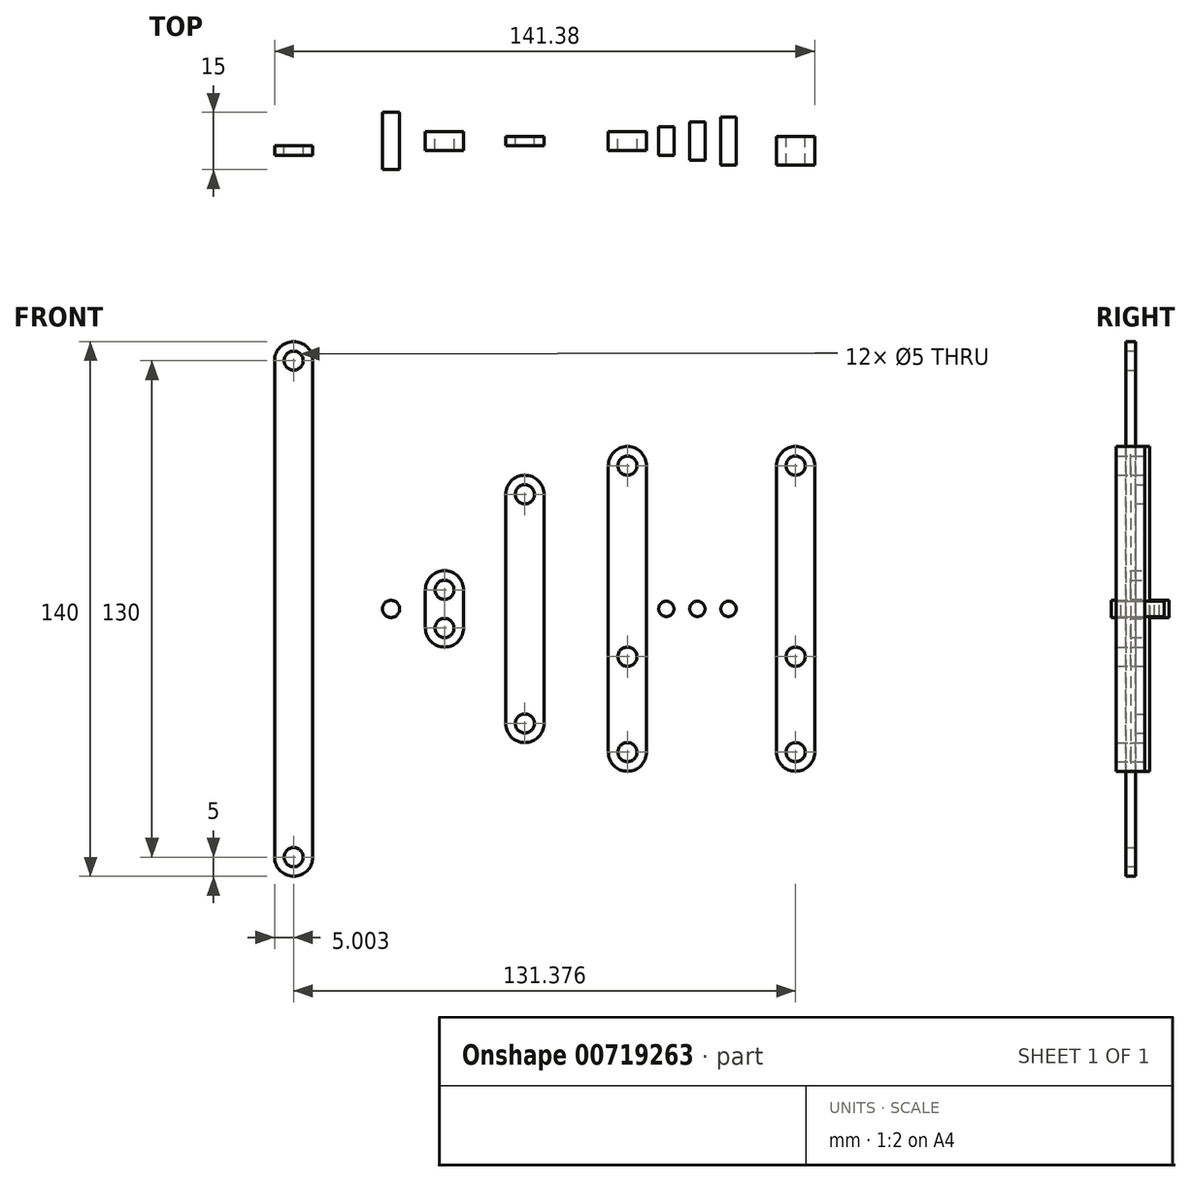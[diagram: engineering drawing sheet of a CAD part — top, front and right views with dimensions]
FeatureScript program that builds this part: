
annotation { "Feature Type Name" : "Feature", "Feature Type Description" : "" }
export const myFeature = defineFeature(function(context is Context, id is Id, definition is map)
    precondition{}
    {
        {
            assignVariable(context, id + "F0", {"name" : "pin1_len", "anyValue" : 7.5});
        }
        {
            assignVariable(context, id + "F1", {"name" : "pin2_len", "anyValue" : 10});
        }
        {
            var Q0;
            Q0=qCreatedBy(makeId("Front.planeOp"),FACE);
            var sketch = newSketch(context, id + "F2", { "sketchPlane" : qUnion([Q0])});
            skLineSegment(sketch, "E0", {"start": v(-5, 0) * mm, "end": v(5, 0) * mm, "construction": true});
            skArc(sketch, "E1", {"start": v(5, 37.5) * mm, "mid": v(0, 42.5) * mm, "end": v(-5, 37.5) * mm});
            skLineSegment(sketch, "E2", {"start": v(5, 37.5) * mm, "end": v(-5, 37.5) * mm, "construction": true});
            skLineSegment(sketch, "E3", {"start": v(-5, 37.5) * mm, "end": v(-5, 0) * mm});
            skLineSegment(sketch, "E4", {"start": v(5, 37.5) * mm, "end": v(5, 0) * mm});
            skCircle(sketch, "E5", {"center": v(0, 37.5) * mm, "radius": 2.5 * mm});
            skArc(sketch, "E6.MirrorCS", {"start": v(5, -37.5) * mm, "mid": v(0, -42.5) * mm, "end": v(-5, -37.5) * mm});
            skCircle(sketch, "E7.MirrorC", {"center": v(0, -37.5) * mm, "radius": 2.5 * mm});
            skLineSegment(sketch, "E8.MirrorCS", {"start": v(-5, -37.5) * mm, "end": v(-5, 0) * mm});
            skLineSegment(sketch, "E9.MirrorCS", {"start": v(5, -37.5) * mm, "end": v(5, 0) * mm});
            skCircle(sketch, "E10", {"center": v(0, -12.5) * mm, "radius": 2.5 * mm});
            skSolve(sketch);
        }
        {
            var Q0;
            Q0 = qSketchRegion(id + "F2", true);
            extrude(context, id + "F3", {"entities" : qUnion([Q0]), "depth" : 5 * mm, "offsetDistance" : 25 * mm, "symmetric" : true});
        }
        {
            var Q0;
            Q0=qCreatedBy(makeId("Front.planeOp"),FACE);
            var sketch = newSketch(context, id + "F4", { "sketchPlane" : qUnion([Q0])});
            skLineSegment(sketch, "E11", {"start": v(-31.86, 0) * mm, "end": v(-21.86, 0) * mm, "construction": true});
            skArc(sketch, "E12", {"start": v(-21.86, 30) * mm, "mid": v(-26.86, 35) * mm, "end": v(-31.86, 30) * mm});
            skLineSegment(sketch, "E13", {"start": v(-21.86, 30) * mm, "end": v(-31.86, 30) * mm, "construction": true});
            skLineSegment(sketch, "E14", {"start": v(-31.86, 30) * mm, "end": v(-31.86, 0) * mm});
            skLineSegment(sketch, "E15", {"start": v(-21.86, 30) * mm, "end": v(-21.86, 0) * mm});
            skCircle(sketch, "E16", {"center": v(-26.86, 30) * mm, "radius": 2.5 * mm});
            skArc(sketch, "E17.MirrorCS", {"start": v(-21.86, -30) * mm, "mid": v(-26.86, -35) * mm, "end": v(-31.86, -30) * mm});
            skCircle(sketch, "E18.MirrorC", {"center": v(-26.86, -30) * mm, "radius": 2.5 * mm});
            skLineSegment(sketch, "E19.MirrorCS", {"start": v(-31.86, -30) * mm, "end": v(-31.86, 0) * mm});
            skLineSegment(sketch, "E20.MirrorCS", {"start": v(-21.86, -30) * mm, "end": v(-21.86, 0) * mm});
            skSolve(sketch);
        }
        {
            var Q0;
            Q0 = qSketchRegion(id + "F4", true);
            extrude(context, id + "F5", {"entities" : qUnion([Q0]), "depth" : 2.5 * mm, "offsetDistance" : 25 * mm, "symmetric" : true});
        }
        {
            var Q0;
            Q0=qCreatedBy(makeId("Front.planeOp"),FACE);
            var sketch = newSketch(context, id + "F6", { "sketchPlane" : qUnion([Q0])});
            skLineSegment(sketch, "E21", {"start": v(-52.87, 0) * mm, "end": v(-42.87, 0) * mm, "construction": true});
            skArc(sketch, "E22", {"start": v(-42.87, 5) * mm, "mid": v(-47.87, 10) * mm, "end": v(-52.87, 5) * mm});
            skLineSegment(sketch, "E23", {"start": v(-42.87, 5) * mm, "end": v(-52.87, 5) * mm, "construction": true});
            skLineSegment(sketch, "E24", {"start": v(-52.87, 5) * mm, "end": v(-52.87, 0) * mm});
            skLineSegment(sketch, "E25", {"start": v(-42.87, 5) * mm, "end": v(-42.87, 0) * mm});
            skCircle(sketch, "E26", {"center": v(-47.87, 5) * mm, "radius": 2.5 * mm});
            skArc(sketch, "E27.MirrorCS", {"start": v(-42.87, -5) * mm, "mid": v(-47.87, -10) * mm, "end": v(-52.87, -5) * mm});
            skCircle(sketch, "E28.MirrorC", {"center": v(-47.87, -5) * mm, "radius": 2.5 * mm});
            skLineSegment(sketch, "E29.MirrorCS", {"start": v(-52.87, -5) * mm, "end": v(-52.87, 0) * mm});
            skLineSegment(sketch, "E30.MirrorCS", {"start": v(-42.87, -5) * mm, "end": v(-42.87, 0) * mm});
            skSolve(sketch);
        }
        {
            var Q0;
            Q0 = qSketchRegion(id + "F6", true);
            extrude(context, id + "F7", {"entities" : qUnion([Q0]), "depth" : 5 * mm, "offsetDistance" : 25 * mm, "symmetric" : true});
        }
        {
            var Q0;
            Q0=qCreatedBy(makeId("Front.planeOp"),FACE);
            var sketch = newSketch(context, id + "F8", { "sketchPlane" : qUnion([Q0])});
            skCircle(sketch, "E31", {"center": v(10.18, 0) * mm, "radius": 2 * mm});
            skSolve(sketch);
        }
        {
            var Q0;
            Q0 = qSketchRegion(id + "F8", true);
            extrude(context, id + "F9", {"entities" : qUnion([Q0]), "depth" : (getVariable(context, 'pin1_len')) * mm, "offsetDistance" : 25 * mm, "symmetric" : true});
        }
        {
            var Q0;
            Q0=qCreatedBy(makeId("Front.planeOp"),FACE);
            var sketch = newSketch(context, id + "F10", { "sketchPlane" : qUnion([Q0])});
            skCircle(sketch, "E32", {"center": v(18.3, 0) * mm, "radius": 2 * mm});
            skSolve(sketch);
        }
        {
            var Q0;
            Q0 = qSketchRegion(id + "F10", true);
            extrude(context, id + "F11", {"entities" : qUnion([Q0]), "depth" : (getVariable(context, 'pin2_len')) * mm, "offsetDistance" : 25 * mm, "symmetric" : true});
        }
        {
            var Q0;
            Q0=makeQuery(id+"F3.opExtrude","CAP_FACE",FACE,{"disambiguationData":[OSD([sQuery(id+"F2.wireOp",EDGE,"E1"),sQuery(id+"F2.wireOp",EDGE,"E3"),sQuery(id+"F2.wireOp",EDGE,"E4"),sQuery(id+"F2.wireOp",EDGE,"E5"),sQuery(id+"F2.wireOp",EDGE,"E6.MirrorCS"),sQuery(id+"F2.wireOp",EDGE,"E7.MirrorC"),sQuery(id+"F2.wireOp",EDGE,"E8.MirrorCS"),sQuery(id+"F2.wireOp",EDGE,"E9.MirrorCS"),sQuery(id+"F2.wireOp",EDGE,"E10")])],"isStart":false});
            var sketch = newSketch(context, id + "F12", { "sketchPlane" : qUnion([Q0])});
            skLineSegment(sketch, "E33", {"start": v(39, 0) * mm, "end": v(49, 0) * mm, "construction": true});
            skArc(sketch, "E34", {"start": v(49, 37.5) * mm, "mid": v(44, 42.5) * mm, "end": v(39, 37.5) * mm});
            skLineSegment(sketch, "E35", {"start": v(49, 37.5) * mm, "end": v(39, 37.5) * mm, "construction": true});
            skLineSegment(sketch, "E36", {"start": v(39, 37.5) * mm, "end": v(39, 0) * mm});
            skLineSegment(sketch, "E37", {"start": v(49, 37.5) * mm, "end": v(49, 0) * mm});
            skCircle(sketch, "E38", {"center": v(44, 37.5) * mm, "radius": 2.5 * mm});
            skArc(sketch, "E39.MirrorCS", {"start": v(49, -37.5) * mm, "mid": v(44, -42.5) * mm, "end": v(39, -37.5) * mm});
            skCircle(sketch, "E40.MirrorC", {"center": v(44, -37.5) * mm, "radius": 2.5 * mm});
            skLineSegment(sketch, "E41.MirrorCS", {"start": v(39, -37.5) * mm, "end": v(39, 0) * mm});
            skLineSegment(sketch, "E42.MirrorCS", {"start": v(49, -37.5) * mm, "end": v(49, 0) * mm});
            skCircle(sketch, "E43", {"center": v(44, -12.5) * mm, "radius": 2.5 * mm});
            skSolve(sketch);
        }
        {
            var Q0;
            Q0 = qSketchRegion(id + "F12", true);
            extrude(context, id + "F13", {"entities" : qUnion([Q0]), "depth" : 7.5 * mm, "offsetDistance" : 25 * mm, "symmetric" : true});
        }
        {
            var Q0;
            Q0=qCreatedBy(makeId("Front.planeOp"),FACE);
            var sketch = newSketch(context, id + "F14", { "sketchPlane" : qUnion([Q0])});
            skCircle(sketch, "E44", {"center": v(26.45, 0) * mm, "radius": 2 * mm});
            skSolve(sketch);
        }
        {
            var Q0;
            Q0=makeQuery(id+"F14.imprint","IMPRINT",FACE,{"disambiguationData":[TD([[makeQuery(id+"F14.imprint","IMPRINT",EDGE,{"derivedFrom":sQuery(id+"F14.wireOp",EDGE,"E44")}),1.0]])]});
            extrude(context, id + "F15", {"entities" : qUnion([Q0]), "depth" : 12.5 * mm, "offsetDistance" : 25 * mm, "symmetric" : true});
        }
        {
            var Q0;
            Q0=qCreatedBy(makeId("Front.planeOp"),FACE);
            var sketch = newSketch(context, id + "F16", { "sketchPlane" : qUnion([Q0])});
            skCircle(sketch, "E45", {"center": v(-61.88, 0) * mm, "radius": 2.25 * mm});
            skSolve(sketch);
        }
        {
            var Q0;
            Q0=makeQuery(id+"F16.imprint","IMPRINT",FACE,{"disambiguationData":[TD([[makeQuery(id+"F16.imprint","IMPRINT",EDGE,{"derivedFrom":sQuery(id+"F16.wireOp",EDGE,"E45")}),1.0]])]});
            extrude(context, id + "F17", {"entities" : qUnion([Q0]), "depth" : 15 * mm, "offsetDistance" : 25 * mm, "symmetric" : true});
        }
        {
            var Q0;
            Q0=makeQuery(id+"F5.opExtrude","CAP_FACE",FACE,{"disambiguationData":[OSD([sQuery(id+"F4.wireOp",EDGE,"E12"),sQuery(id+"F4.wireOp",EDGE,"E14"),sQuery(id+"F4.wireOp",EDGE,"E15"),sQuery(id+"F4.wireOp",EDGE,"E16"),sQuery(id+"F4.wireOp",EDGE,"E17.MirrorCS"),sQuery(id+"F4.wireOp",EDGE,"E18.MirrorC"),sQuery(id+"F4.wireOp",EDGE,"E19.MirrorCS"),sQuery(id+"F4.wireOp",EDGE,"E20.MirrorCS")])],"isStart":false});
            var sketch = newSketch(context, id + "F18", { "sketchPlane" : qUnion([Q0])});
            skLineSegment(sketch, "E46", {"start": v(-92.37, 0) * mm, "end": v(-82.37, 0) * mm, "construction": true});
            skArc(sketch, "E47", {"start": v(-82.37, 65) * mm, "mid": v(-87.37, 70) * mm, "end": v(-92.37, 65) * mm});
            skLineSegment(sketch, "E48", {"start": v(-82.37, 65) * mm, "end": v(-92.37, 65) * mm, "construction": true});
            skLineSegment(sketch, "E49", {"start": v(-92.37, 65) * mm, "end": v(-92.37, 0) * mm});
            skLineSegment(sketch, "E50", {"start": v(-82.37, 65) * mm, "end": v(-82.37, 0) * mm});
            skCircle(sketch, "E51", {"center": v(-87.37, 65) * mm, "radius": 2.5 * mm});
            skArc(sketch, "E52.MirrorCS", {"start": v(-82.37, -65) * mm, "mid": v(-87.37, -70) * mm, "end": v(-92.37, -65) * mm});
            skCircle(sketch, "E53.MirrorC", {"center": v(-87.37, -65) * mm, "radius": 2.5 * mm});
            skLineSegment(sketch, "E54.MirrorCS", {"start": v(-92.37, -65) * mm, "end": v(-92.37, 0) * mm});
            skLineSegment(sketch, "E55.MirrorCS", {"start": v(-82.37, -65) * mm, "end": v(-82.37, 0) * mm});
            skSolve(sketch);
        }
        {
            var Q0;
            Q0 = qSketchRegion(id + "F18", true);
            extrude(context, id + "F19", {"entities" : qUnion([Q0]), "depth" : 2.5 * mm, "offsetDistance" : 25 * mm});
        }
    });
